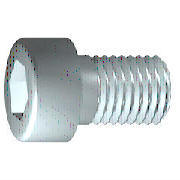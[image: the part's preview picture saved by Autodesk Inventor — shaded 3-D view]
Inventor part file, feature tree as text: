
AUTODESK INVENTOR PART (.ipt)
format: ipt  version: 2020 (Build 240168000, 168)  size: 188,928 bytes
history: native  units: mm (DEFAULTED — no unit token found)
features: sketch x2, extrude x1, plane x1, fillet x1
ambient origin geometry x7: Origin, YZ Plane, XY Plane, X Axis, Y Axis, Z Axis, Center Point
bodies: Solid1 (feature_tree), Body (feature_tree)
feature tree (5):
  extrude  "Slot"  Depth=3.0mm
  plane  "Work Plane1"
  fillet  "Fillet2"  Radius=3.0mm
  sketch  "Sketch1"  dims[d1=18.0mm d2=0.306825mm d3=3.0mm]
  sketch  "Sketch2"  dims[d4=1.3mm d5=60.0deg d6=3.0mm d7=3.0mm d8=2.886751mm d9=5.5mm d10=90.0deg d11=10.0mm d12=0.0mm d13=18.0mm d14=0.0mm d15=0.306725mm d16=0.306725mm d17=0.3mm d19=0.0mm d26=25.0mm d27=45.0deg d28=0.0mm d29=0.0mm d30=0.1mm]
